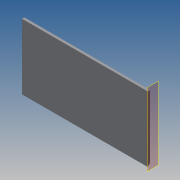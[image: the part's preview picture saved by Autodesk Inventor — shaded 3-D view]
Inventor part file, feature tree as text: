
AUTODESK INVENTOR PART (.ipt)
format: ipt  version: 2013 (Build 170138000, 138)  size: 169,984 bytes
history: native  units: in
note: dims shown in document units (in); Inventor stores cm internally (conversion verified against a paired STEP export)
features: extrude x8, sketch x8, reference x8, plane x2, chamfer x1
ambient origin geometry x8: Origin, YZ Plane, XZ Plane, XY Plane, X Axis, Y Axis, Z Axis, Center Point
bodies: Solid1 (feature_tree)
feature tree (27):
  plane  "Work Plane1"
  extrude  "Extrusion1"  Depth=0.0098in
  extrude  "Extrusion2"  Depth=0.0394in
  chamfer  "Chamfer1"  Distance=105.7in
  extrude  "Extrusion3"  Depth=105.7in TaperAngle=0.0deg
  sketch  "Sketch4"  dims[d12=0.2362in d14=105.7in d15=0.0in]
  plane  "Work Plane2"
  extrude  "Extrusion4"  Depth=105.7in TaperAngle=0.0deg
  extrude  "Extrusion5"  Depth=0.0197in TaperAngle=0.0deg
  extrude  "Extrusion6"  Depth=0.5in TaperAngle=0.0deg
  extrude  "Extrusion7"  Depth=0.0315in
  extrude  "Extrusion8"  [1 undecoded]
  sketch  "Sketch1"  dims[d0=0.0098in d1=0.0098in]
  reference  "Reference1"
  reference  "Reference2"
  sketch  "Sketch2"  dims[d2=4.1614in d3=0.0in d4=0.0394in d5=105.7in d6=0.0in]
  reference  "Reference3"
  reference  "Reference4"
  sketch  "Sketch3"  dims[d7=0.0787in d8=0.125in d9=45.0deg d10=105.7in d11=0.0in]
  reference  "Reference5"
  sketch  "Sketch5"  dims[d16=0.0in d17=0.0in d18=0.0197in d19=0.0in]
  sketch  "Sketch6"  dims[d20=0.1181in d22=0.5in d23=0.0in]
  sketch  "Sketch7"  dims[d24=0.0315in d25=0.0315in]
  reference  "Reference6"
  reference  "Reference7"
  reference  "Reference8"
  sketch  "Sketch8"  dims[d26=0.5in d27=0.0in]
note: 1 required parameter value undecoded (feature->parameter linkage not recoverable at this tier; creation-order binding heuristic only, values carry confidence <= 0.55)
